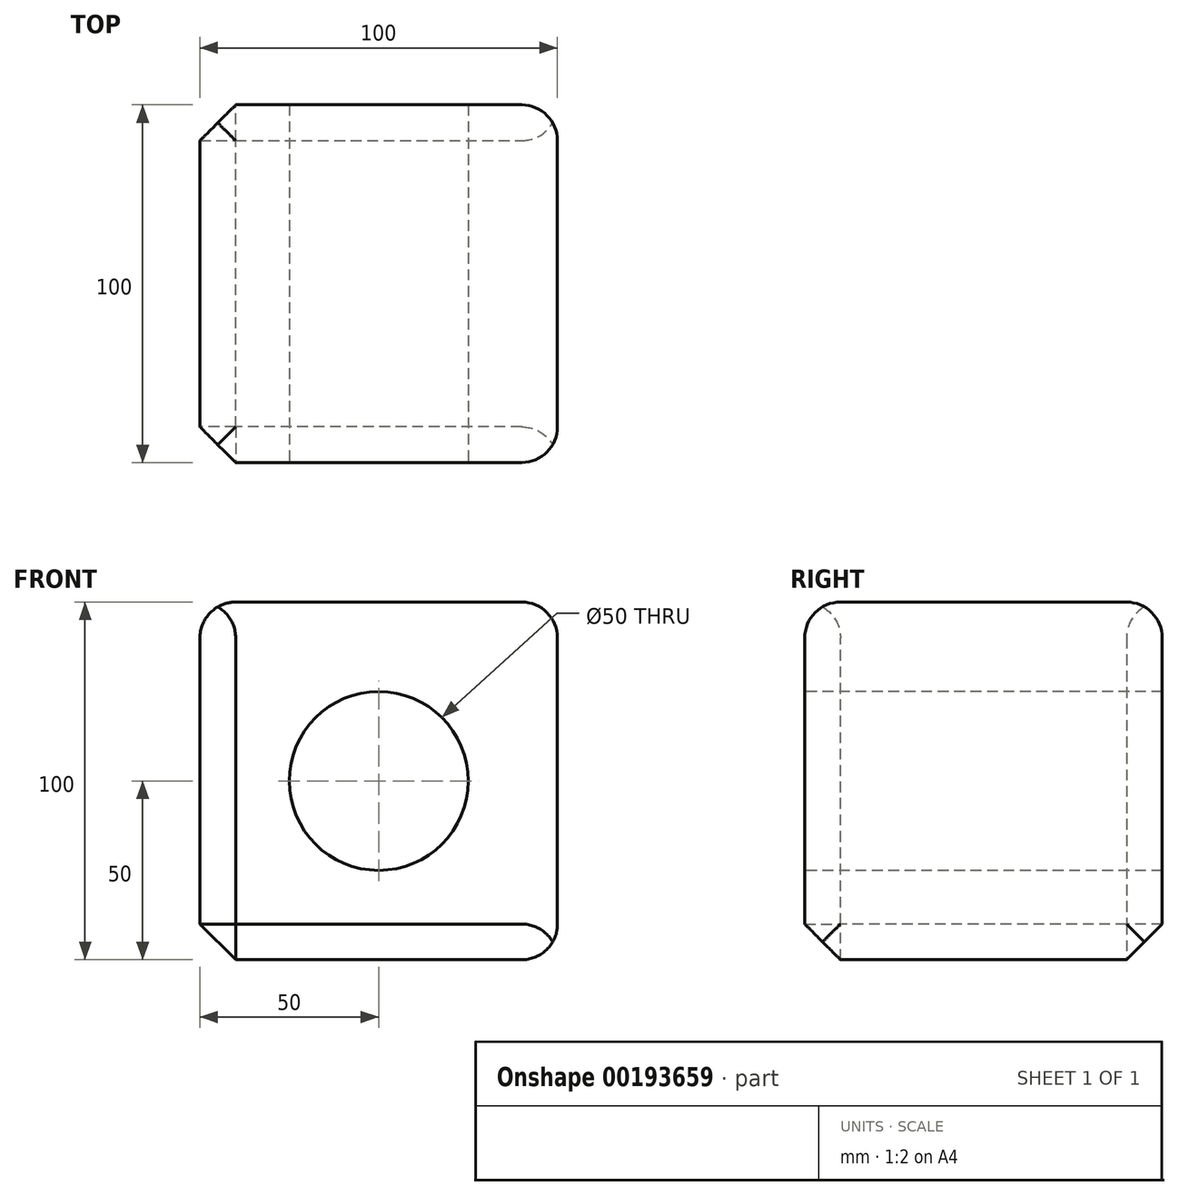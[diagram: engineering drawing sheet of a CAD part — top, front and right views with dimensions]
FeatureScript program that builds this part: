
annotation { "Feature Type Name" : "Feature", "Feature Type Description" : "" }
export const myFeature = defineFeature(function(context is Context, id is Id, definition is map)
    precondition{}
    {
        {
            var Q0;
            Q0=qCreatedBy(makeId("Top.planeOp"),FACE);
            var sketch = newSketch(context, id + "F0", { "sketchPlane" : qUnion([Q0])});
            skLineSegment(sketch, "E0.bottom", {"start": v(50, 50) * mm, "end": v(-50, 50) * mm});
            skLineSegment(sketch, "E0.top", {"start": v(50, -50) * mm, "end": v(-50, -50) * mm});
            skLineSegment(sketch, "E0.left", {"start": v(50, 50) * mm, "end": v(50, -50) * mm});
            skLineSegment(sketch, "E0.right", {"start": v(-50, 50) * mm, "end": v(-50, -50) * mm});
            skPoint(sketch, "E0.middle", {"position": v(0, 0) * mm});
            skSolve(sketch);
        }
        {
            var Q0;
            Q0 = qSketchRegion(id + "F0", true);
            extrude(context, id + "F1", {"entities" : qUnion([Q0]), "depth" : 100 * mm});
        }
        {
            var Q0;
            Q0=makeQuery(id+"F1.opExtrude","SWEPT_FACE",FACE,{"disambiguationData":[OSD([sQuery(id+"F0.wireOp",EDGE,"E0.top")])]});
            var sketch = newSketch(context, id + "F2", { "sketchPlane" : qUnion([Q0])});
            skCircle(sketch, "E1", {"center": v(0, 50) * mm, "radius": 25 * mm});
            skSolve(sketch);
        }
        {
            var Q0;
            Q0=makeQuery(id+"F2.imprint","IMPRINT",FACE,{"disambiguationData":[TD([[makeQuery(id+"F2.imprint","IMPRINT",EDGE,{"derivedFrom":sQuery(id+"F2.wireOp",EDGE,"E1")}),1.0]])]});
            extrude(context, id + "F3", {"entities" : qUnion([Q0]), "operationType" : NewBodyOperationType.REMOVE, "oppositeDirection" : true, "depth" : 264 * mm, "hasSecondDirection" : true, "secondDirectionOppositeDirection" : false, "secondDirectionDepth" : 25 * mm});
        }
        {
            var Q0;
            Q0=makeQuery(id+"F1.opExtrude","SWEPT_FACE",FACE,{"disambiguationData":[OSD([sQuery(id+"F0.wireOp",EDGE,"E0.left")])]});
            var Q1;
            Q1=makeQuery(id+"F1.opExtrude","CAP_FACE",FACE,{"disambiguationData":[OSD([sQuery(id+"F0.wireOp",EDGE,"E0.bottom"),sQuery(id+"F0.wireOp",EDGE,"E0.top"),sQuery(id+"F0.wireOp",EDGE,"E0.left"),sQuery(id+"F0.wireOp",EDGE,"E0.right")])],"isStart":false});
            fillet(context, id + "F4", {"entities" : qUnion([Q0, Q1]), "radius" : 10 * mm, "tangentPropagation" : true, "allowEdgeOverflow" : false});
        }
        {
            var Q0;
            Q0=makeQuery(id+"F1.opExtrude","CAP_FACE",FACE,{"disambiguationData":[OSD([sQuery(id+"F0.wireOp",EDGE,"E0.bottom"),sQuery(id+"F0.wireOp",EDGE,"E0.top"),sQuery(id+"F0.wireOp",EDGE,"E0.left"),sQuery(id+"F0.wireOp",EDGE,"E0.right")])],"isStart":true});
            var Q1;
            Q1=makeQuery(id+"F1.opExtrude","SWEPT_FACE",FACE,{"disambiguationData":[OSD([sQuery(id+"F0.wireOp",EDGE,"E0.right")])]});
            chamfer(context, id + "F5", {"entities" : qUnion([Q0, Q1]), "width" : 10 * mm, "tangentPropagation" : true});
        }
    });
